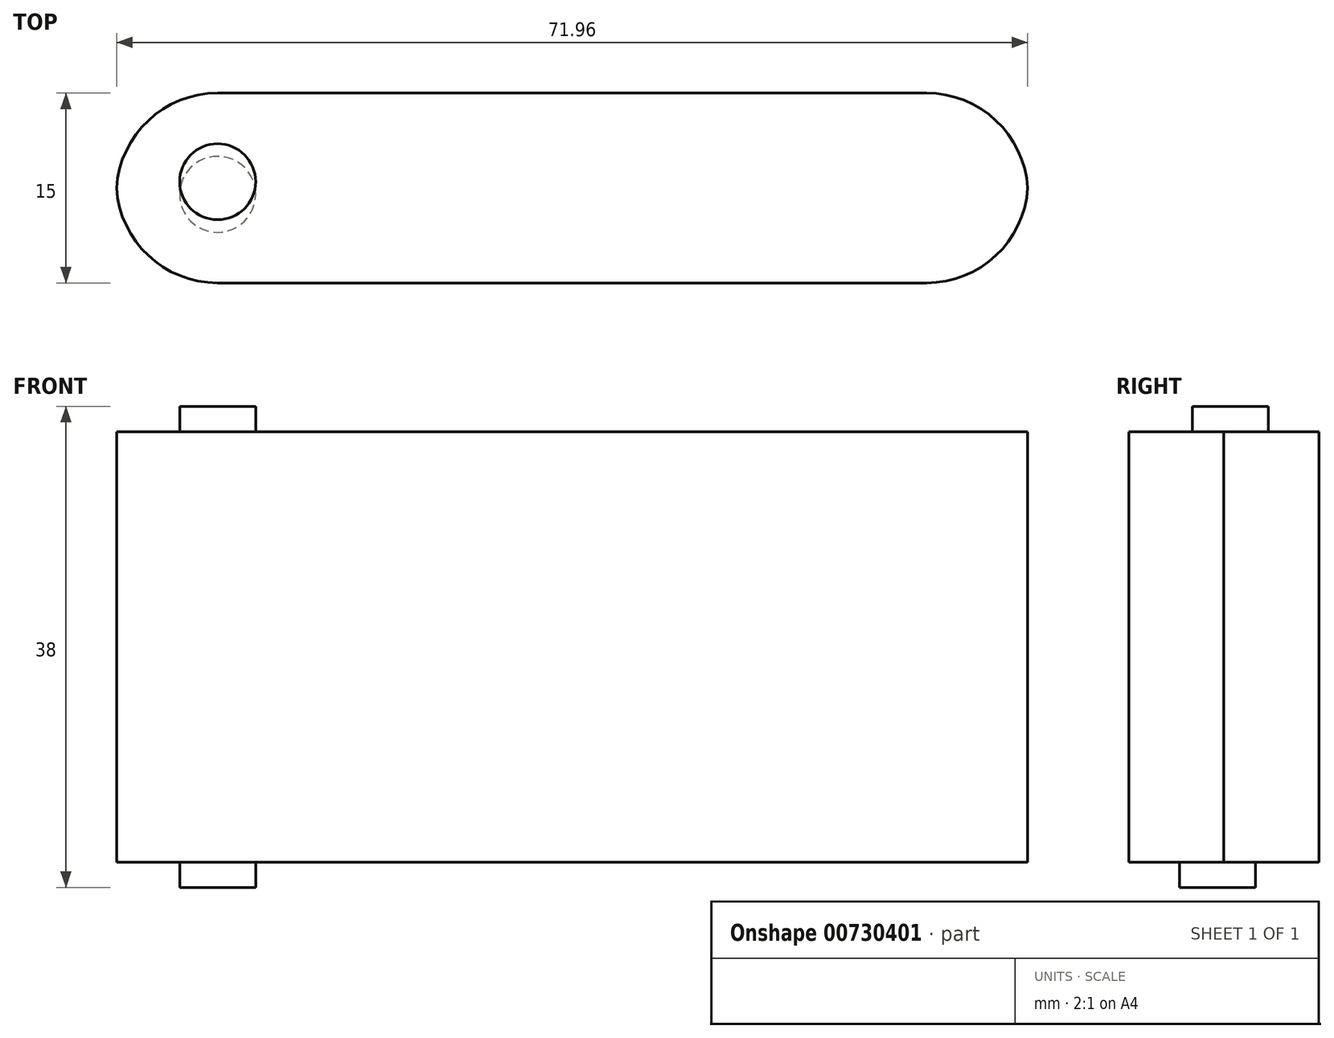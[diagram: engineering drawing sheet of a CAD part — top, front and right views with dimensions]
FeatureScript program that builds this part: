
annotation { "Feature Type Name" : "Feature", "Feature Type Description" : "" }
export const myFeature = defineFeature(function(context is Context, id is Id, definition is map)
    precondition{}
    {
        {
            var Q0;
            Q0=qCreatedBy(makeId("Front.planeOp"),FACE);
            var sketch = newSketch(context, id + "F0", { "sketchPlane" : qUnion([Q0])});
            skLineSegment(sketch, "E0.bottom", {"start": v(-36, -17) * mm, "end": v(36, -17) * mm});
            skLineSegment(sketch, "E0.top", {"start": v(-36, 17) * mm, "end": v(36, 17) * mm});
            skLineSegment(sketch, "E0.left", {"start": v(-36, -17) * mm, "end": v(-36, 17) * mm});
            skLineSegment(sketch, "E0.right", {"start": v(36, -17) * mm, "end": v(36, 17) * mm});
            skPoint(sketch, "E0.middle", {"position": v(0, 0) * mm});
            skSolve(sketch);
        }
        {
            var Q0;
            Q0 = qSketchRegion(id + "F0", true);
            extrude(context, id + "F1", {"entities" : qUnion([Q0]), "depth" : 15 * mm, "offsetDistance" : 25 * mm});
        }
        {
            var Q0;
            Q0=makeQuery(id+"F1.opExtrude","CAP_EDGE",EDGE,{"disambiguationData":[OSD([sQuery(id+"F0.wireOp",EDGE,"E0.left")])],"isStart":true});
            var Q1;
            Q1=makeQuery(id+"F1.opExtrude","CAP_EDGE",EDGE,{"disambiguationData":[OSD([sQuery(id+"F0.wireOp",EDGE,"E0.left")])],"isStart":false});
            var Q2;
            Q2=makeQuery(id+"F1.opExtrude","CAP_EDGE",EDGE,{"disambiguationData":[OSD([sQuery(id+"F0.wireOp",EDGE,"E0.right")])],"isStart":false});
            var Q3;
            Q3=makeQuery(id+"F1.opExtrude","CAP_EDGE",EDGE,{"disambiguationData":[OSD([sQuery(id+"F0.wireOp",EDGE,"E0.right")])],"isStart":true});
            fillet(context, id + "F2", {"entities" : qUnion([Q0, Q1, Q2, Q3]), "radius" : 8 * mm, "tangentPropagation" : true, "allowEdgeOverflow" : false});
        }
        {
            var Q0;
            Q0=makeQuery(id+"F1.opExtrude","SWEPT_FACE",FACE,{"disambiguationData":[OSD([sQuery(id+"F0.wireOp",EDGE,"E0.top")])]});
            var sketch = newSketch(context, id + "F3", { "sketchPlane" : qUnion([Q0])});
            skCircle(sketch, "E1", {"center": v(-28, -7) * mm, "radius": 3 * mm});
            skSolve(sketch);
        }
        {
            var Q0;
            Q0 = qSketchRegion(id + "F3", true);
            extrude(context, id + "F4", {"entities" : qUnion([Q0]), "operationType" : NewBodyOperationType.ADD, "depth" : 2 * mm, "offsetDistance" : 25 * mm});
        }
        {
            var Q0;
            Q0=makeQuery(id+"F1.opExtrude","SWEPT_FACE",FACE,{"disambiguationData":[OSD([sQuery(id+"F0.wireOp",EDGE,"E0.bottom")])]});
            var sketch = newSketch(context, id + "F5", { "sketchPlane" : qUnion([Q0])});
            skCircle(sketch, "E2", {"center": v(-28, 8) * mm, "radius": 3 * mm});
            skSolve(sketch);
        }
        {
            var Q0;
            Q0 = qSketchRegion(id + "F5", true);
            extrude(context, id + "F6", {"entities" : qUnion([Q0]), "operationType" : NewBodyOperationType.ADD, "depth" : 2 * mm, "offsetDistance" : 25 * mm});
        }
    });
